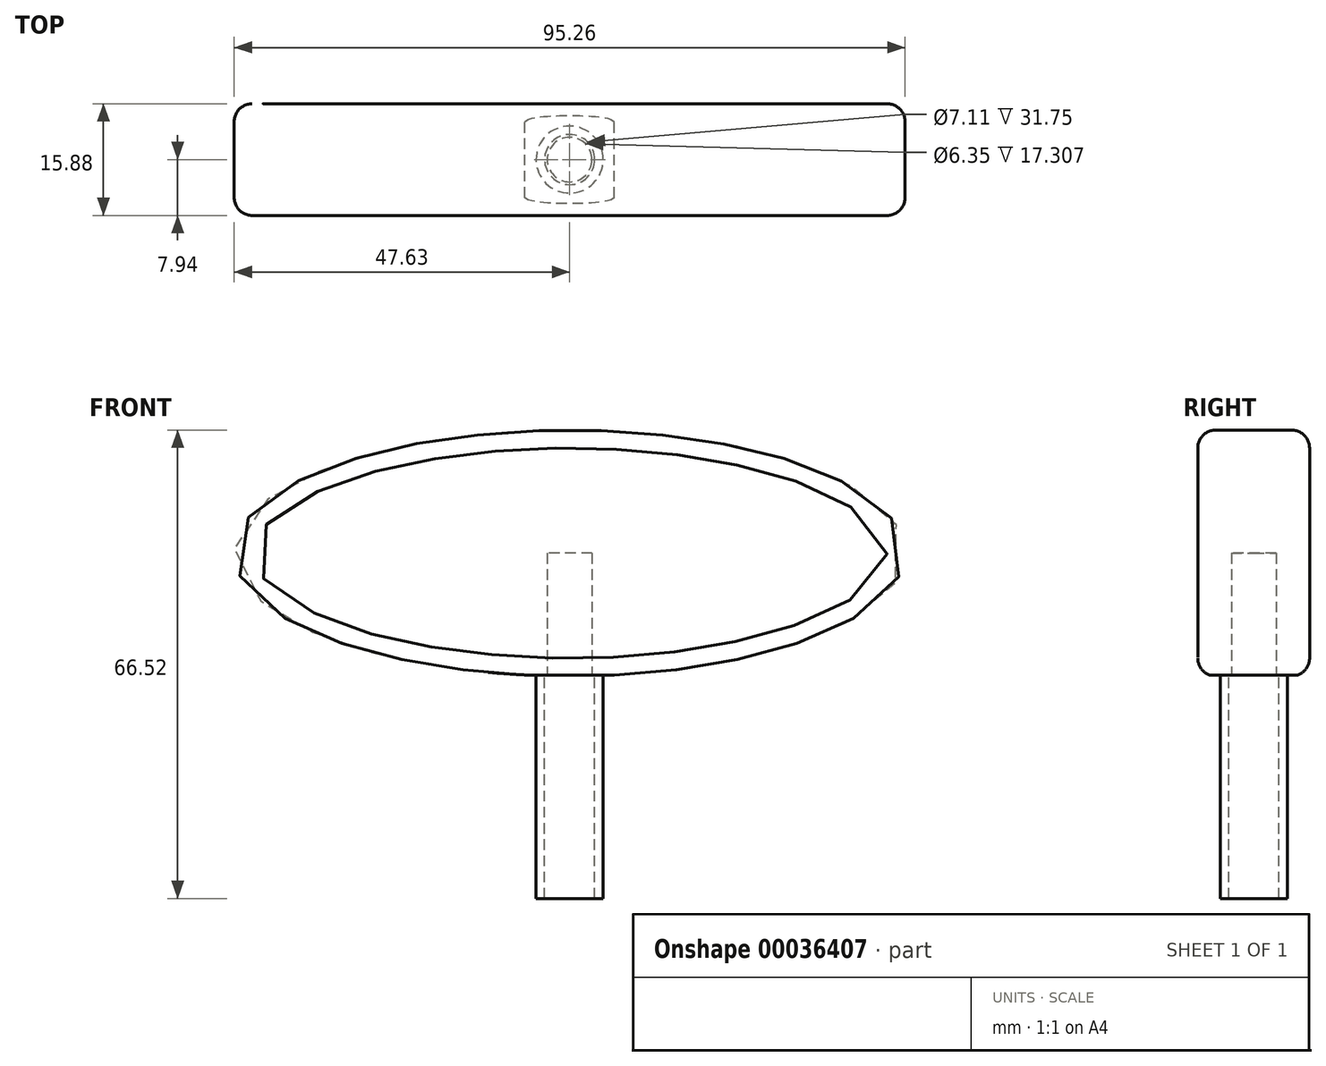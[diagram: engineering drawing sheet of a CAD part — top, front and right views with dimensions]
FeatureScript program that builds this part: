
annotation { "Feature Type Name" : "Feature", "Feature Type Description" : "" }
export const myFeature = defineFeature(function(context is Context, id is Id, definition is map)
    precondition{}
    {
        {
            var Q0;
            Q0=qCreatedBy(makeId("Front.planeOp"),FACE);
            var sketch = newSketch(context, id + "F0", { "sketchPlane" : qUnion([Q0])});
            skEllipticalArc(sketch, "E0", {});
            skLineSegment(sketch, "E1", {"start": v(-6.35, -17.3) * mm, "end": v(6.35, -17.3) * mm});
            const initialGuessF0  = {"E0": [0, 0, -1, 0, 0.047625, 0.017462500000000002, 1.7045279162048372, 1.437064737384954]};
            skSetInitialGuess(sketch, initialGuessF0);
            skSolve(sketch);
        }
        {
            var Q0;
            Q0 = qSketchRegion(id + "F0", true);
            extrude(context, id + "F1", {"entities" : qUnion([Q0]), "endBound" : BoundingType.SYMMETRIC, "depth" : 15.88 * mm});
        }
        {
            var Q0;
            Q0=makeQuery(id+"F1.opExtrude","CAP_EDGE",EDGE,{"disambiguationData":[OSD([sQuery(id+"F0.wireOp",EDGE,"E0")])],"isStart":false});
            var Q1;
            Q1=makeQuery(id+"F1.opExtrude","CAP_EDGE",EDGE,{"disambiguationData":[OSD([sQuery(id+"F0.wireOp",EDGE,"E0")])],"isStart":true});
            fillet(context, id + "F2", {"entities" : qUnion([Q0, Q1]), "radius" : 2.54 * mm, "tangentPropagation" : true, "allowEdgeOverflow" : false});
        }
        {
            var Q0;
            Q0=qCreatedBy(makeId("Top.planeOp"),FACE);
            cPlane(context, id + "F3", {"entities" : qUnion([Q0]), "cplaneType" : CPlaneType.OFFSET, "offset" : 25.4 * mm, "oppositeDirection" : true, "width" : 152.4 * mm, "height" : 152.4 * mm});
        }
        {
            var Q0;
            Q0=qCreatedBy(id+"F3.planeOp",FACE);
            var sketch = newSketch(context, id + "F4", { "sketchPlane" : qUnion([Q0])});
            skCircle(sketch, "E2", {"center": v(0, 0) * mm, "radius": 3.18 * mm});
            skSolve(sketch);
        }
        {
            var Q0;
            Q0 = qSketchRegion(id + "F4", true);
            extrude(context, id + "F5", {"entities" : qUnion([Q0]), "operationType" : NewBodyOperationType.REMOVE, "depth" : 25.4 * mm});
        }
        {
            var Q0;
            Q0=makeQuery(id+"F1.opExtrude","SWEPT_FACE",FACE,{"disambiguationData":[OSD([sQuery(id+"F0.wireOp",EDGE,"E1")])]});
            var sketch = newSketch(context, id + "F6", { "sketchPlane" : qUnion([Q0])});
            skCircle(sketch, "E3", {"center": v(0, 0) * mm, "radius": 3.56 * mm});
            skCircle(sketch, "E4", {"center": v(0, 0) * mm, "radius": 4.76 * mm});
            skSolve(sketch);
        }
        {
            var Q0;
            Q0 = qSketchRegion(id + "F6", true);
            extrude(context, id + "F7", {"entities" : qUnion([Q0]), "depth" : 31.75 * mm});
        }
    });
